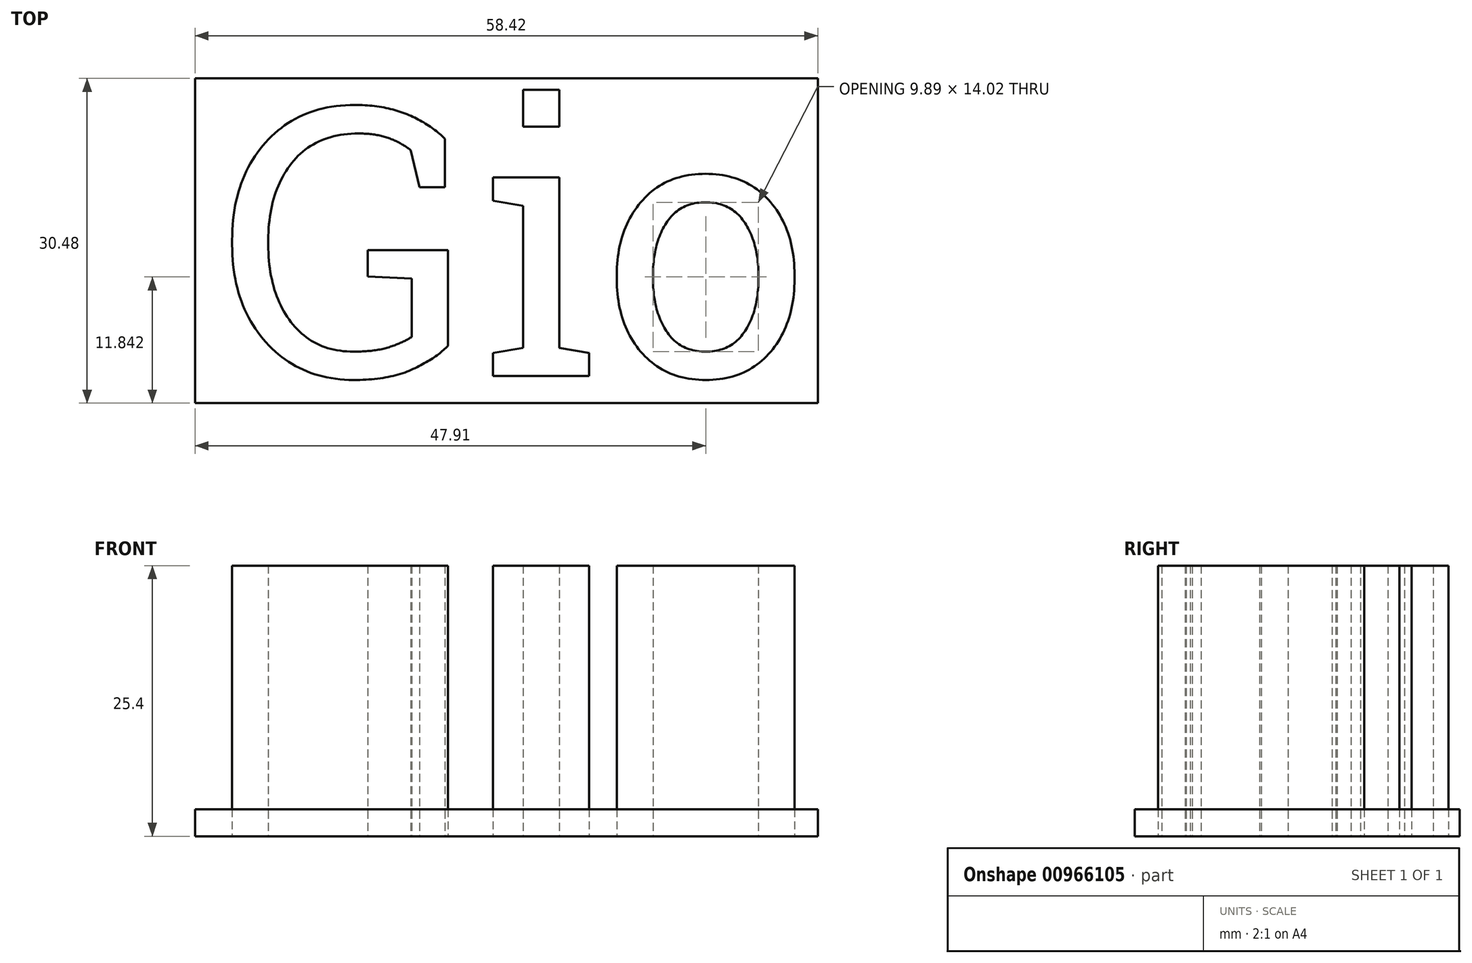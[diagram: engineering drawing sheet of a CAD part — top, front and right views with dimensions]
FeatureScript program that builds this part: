
annotation { "Feature Type Name" : "Feature", "Feature Type Description" : "" }
export const myFeature = defineFeature(function(context is Context, id is Id, definition is map)
    precondition{}
    {
        {
            var Q0;
            Q0=qCreatedBy(makeId("Top.planeOp"),FACE);
            var sketch = newSketch(context, id + "F0", { "sketchPlane" : qUnion([Q0])});
            skText(sketch, "E0", { "text": "Gio", "fontName": "RobotoSlab-Regular.ttf"});
            const initialGuessF0  = {"E0": [0, 0, 1, 0, 0.0254]};
            skSetInitialGuess(sketch, initialGuessF0);
            skSolve(sketch);
        }
        {
            var Q0;
            Q0 = qSketchRegion(id + "F0", true);
            extrude(context, id + "F1", {"entities" : qUnion([Q0]), "depth" : 25.4 * mm, "offsetDistance" : 25.4 * mm});
        }
        {
            var Q0;
            Q0=qCreatedBy(makeId("Top.planeOp"),FACE);
            var sketch = newSketch(context, id + "F2", { "sketchPlane" : qUnion([Q0])});
            skLineSegment(sketch, "E1.bottom", {"start": v(-2.54, -2.54) * mm, "end": v(55.88, -2.54) * mm});
            skLineSegment(sketch, "E1.top", {"start": v(-2.54, 27.94) * mm, "end": v(55.88, 27.94) * mm});
            skLineSegment(sketch, "E1.left", {"start": v(-2.54, -2.54) * mm, "end": v(-2.54, 27.94) * mm});
            skLineSegment(sketch, "E1.right", {"start": v(55.88, -2.54) * mm, "end": v(55.88, 27.94) * mm});
            skSolve(sketch);
        }
        {
            var Q0;
            Q0 = qSketchRegion(id + "F2", true);
            extrude(context, id + "F3", {"entities" : qUnion([Q0]), "depth" : 2.54 * mm, "offsetDistance" : 25.4 * mm});
        }
    });
